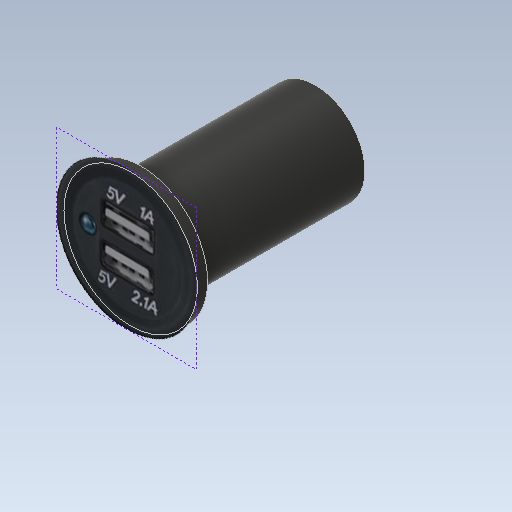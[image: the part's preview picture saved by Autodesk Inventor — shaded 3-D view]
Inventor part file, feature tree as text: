
AUTODESK INVENTOR PART (.ipt)
format: ipt  version: 2021 (Build 250183000, 183)  size: 179,200 bytes
history: native  units: mm
features: sketch x3, extrude x2, other x1
ambient origin geometry x8: Origin, YZ Plane, XZ Plane, XY Plane, X Axis, Y Axis, Z Axis, Center Point
bodies: Solid1 (feature_tree)
feature tree (6):
  extrude  "Extrusion1"  Depth=51.0mm TaperAngle=0.0deg
  extrude  "Extrusion2"  Depth=3.0mm TaperAngle=0.0deg
  sketch  "Sketch3"
  sketch  "Sketch1"  dims[d0=29.0mm d1=51.0mm d2=0.0mm]
  sketch  "Sketch2"  dims[d3=5.0mm d4=3.0mm d5=0.0mm]
  other  "Image1"
